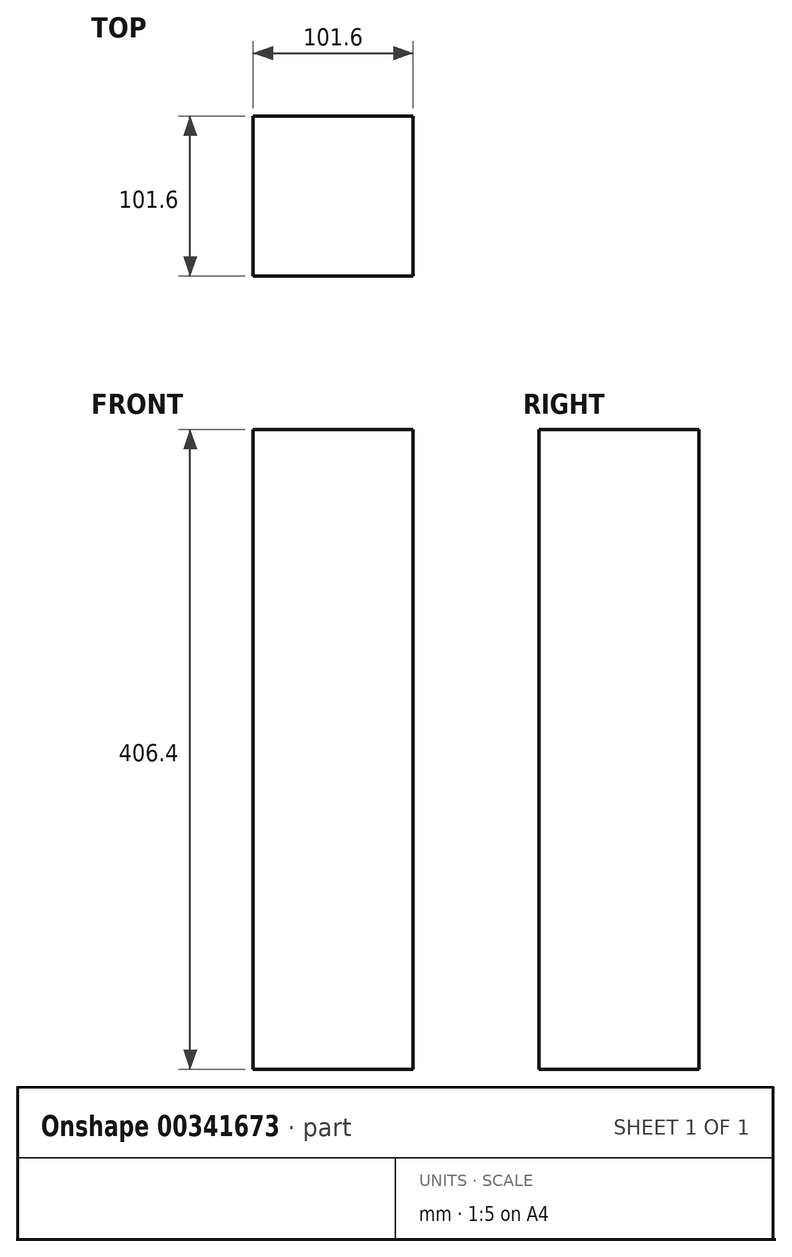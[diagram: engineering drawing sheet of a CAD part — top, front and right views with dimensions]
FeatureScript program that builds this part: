
annotation { "Feature Type Name" : "Feature", "Feature Type Description" : "" }
export const myFeature = defineFeature(function(context is Context, id is Id, definition is map)
    precondition{}
    {
        {
            var Q0;
            Q0=qCreatedBy(makeId("Front.planeOp"),FACE);
            var sketch = newSketch(context, id + "F0", { "sketchPlane" : qUnion([Q0])});
            skLineSegment(sketch, "E0.bottom", {"start": v(-54.25, 332.85) * mm, "end": v(47.35, 332.85) * mm});
            skLineSegment(sketch, "E0.top", {"start": v(-54.25, -73.55) * mm, "end": v(47.35, -73.55) * mm});
            skLineSegment(sketch, "E0.left", {"start": v(-54.25, 332.85) * mm, "end": v(-54.25, -73.55) * mm});
            skLineSegment(sketch, "E0.right", {"start": v(47.35, 332.85) * mm, "end": v(47.35, -73.55) * mm});
            skSolve(sketch);
        }
        {
            var Q0;
            Q0=makeQuery(id+"F0.imprint","IMPRINT",FACE,{"disambiguationData":[TD([[makeQuery(id+"F0.imprint","IMPRINT",EDGE,{"derivedFrom":sQuery(id+"F0.wireOp",EDGE,"E0.bottom")}),-1.0]])]});
            extrude(context, id + "F1", {"entities" : qUnion([Q0]), "depth" : 101.6 * mm, "offsetDistance" : 25.4 * mm});
        }
    });
